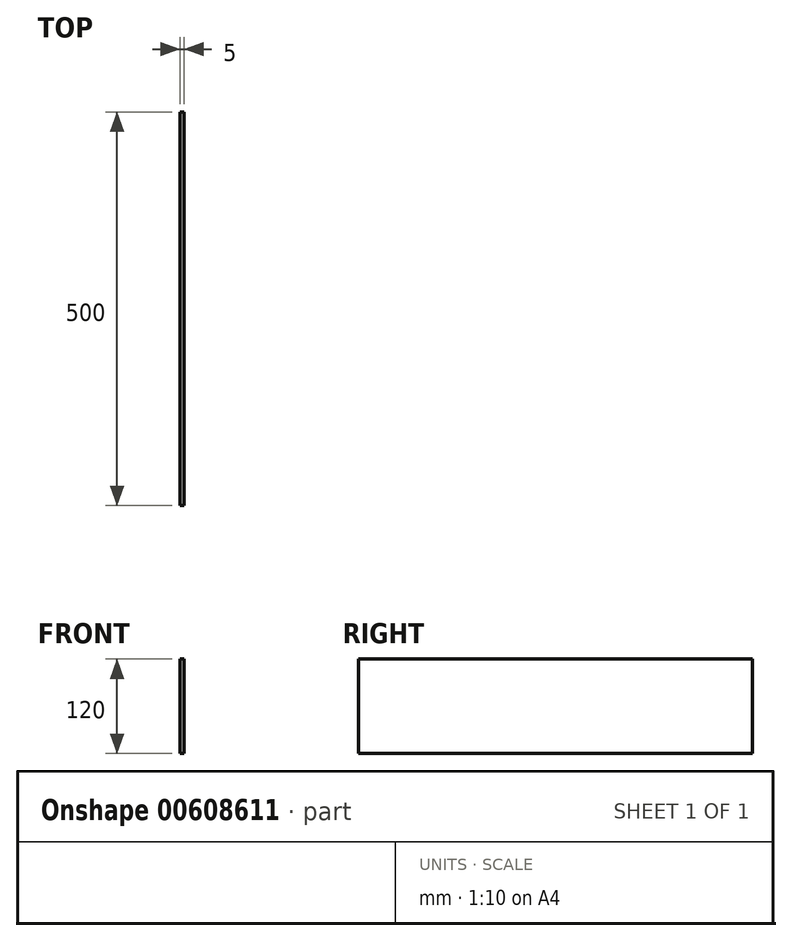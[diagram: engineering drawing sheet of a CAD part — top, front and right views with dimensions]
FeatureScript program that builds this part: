
annotation { "Feature Type Name" : "Feature", "Feature Type Description" : "" }
export const myFeature = defineFeature(function(context is Context, id is Id, definition is map)
    precondition{}
    {
        {
            var Q0;
            Q0=qCreatedBy(makeId("Right.planeOp"),FACE);
            var sketch = newSketch(context, id + "F0", { "sketchPlane" : qUnion([Q0])});
            skLineSegment(sketch, "E0.bottom", {"start": v(0, 0) * mm, "end": v(500, 0) * mm});
            skLineSegment(sketch, "E0.top", {"start": v(0, 120) * mm, "end": v(500, 120) * mm});
            skLineSegment(sketch, "E0.left", {"start": v(0, 0) * mm, "end": v(0, 120) * mm});
            skLineSegment(sketch, "E0.right", {"start": v(500, 0) * mm, "end": v(500, 120) * mm});
            skSolve(sketch);
        }
        {
            var Q0;
            Q0 = qSketchRegion(id + "F0", true);
            extrude(context, id + "F1", {"entities" : qUnion([Q0]), "depth" : 5 * mm, "offsetDistance" : 25 * mm});
        }
    });
